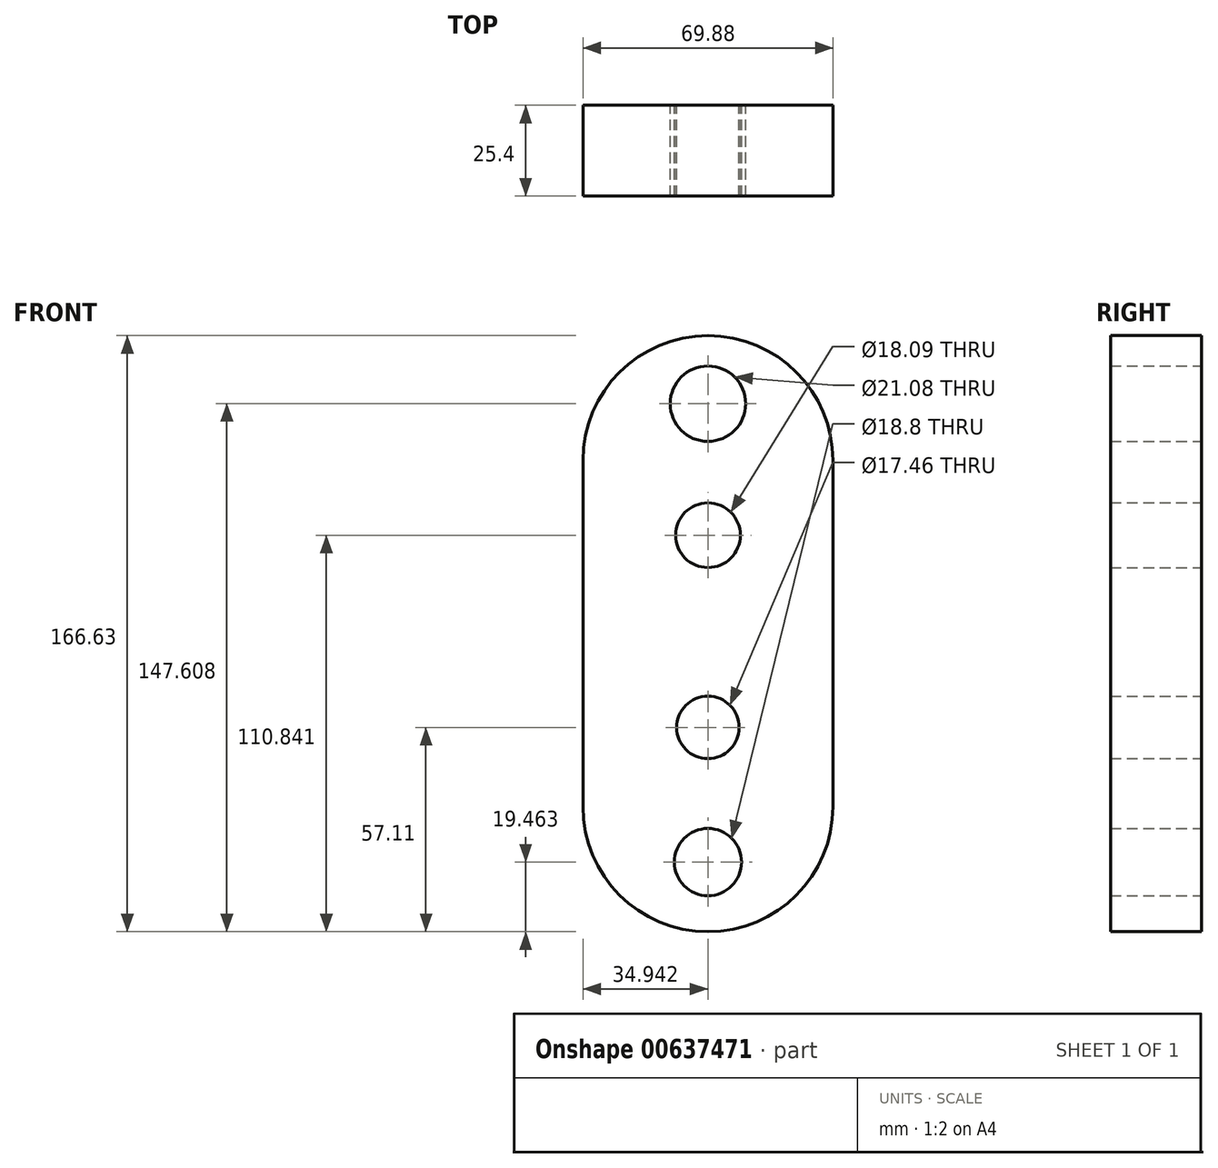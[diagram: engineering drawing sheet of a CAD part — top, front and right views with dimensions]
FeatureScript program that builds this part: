
annotation { "Feature Type Name" : "Feature", "Feature Type Description" : "" }
export const myFeature = defineFeature(function(context is Context, id is Id, definition is map)
    precondition{}
    {
        {
            var Q0;
            Q0=qCreatedBy(makeId("Front.planeOp"),FACE);
            var sketch = newSketch(context, id + "F0", { "sketchPlane" : qUnion([Q0])});
            skLineSegment(sketch, "E0", {"start": v(-48, 38.17) * mm, "end": v(-48, -33.18) * mm});
            skLineSegment(sketch, "E1", {"start": v(-17.47, 38.17) * mm, "end": v(-17.47, -33.18) * mm});
            skArc(sketch, "E2", {"start": v(-17.47, 38.17) * mm, "mid": v(-32.74, 53.44) * mm, "end": v(-48, 38.17) * mm});
            skArc(sketch, "E3", {"start": v(-48, -33.18) * mm, "mid": v(-32.74, -43.31) * mm, "end": v(-17.47, -33.18) * mm});
            skCircle(sketch, "E4", {"center": v(-32.74, 32.6) * mm, "radius": 9.05 * mm});
            skCircle(sketch, "E5", {"center": v(-32.74, -21.14) * mm, "radius": 8.73 * mm});
            skLineSegment(sketch, "E6", {"start": v(-67.68, 53.44) * mm, "end": v(-67.68, -43.31) * mm});
            skPoint(sketch, "E6.startSnap0", {"position": v(-32.74, 53.44) * mm});
            skPoint(sketch, "E6.endSnap0", {"position": v(-32.74, -43.31) * mm});
            skLineSegment(sketch, "E7", {"start": v(2.2, 53.44) * mm, "end": v(2.2, -43.31) * mm});
            skArc(sketch, "E8", {"start": v(2.2, 53.44) * mm, "mid": v(-32.74, 88.38) * mm, "end": v(-67.68, 53.44) * mm});
            skArc(sketch, "E9", {"start": v(-67.68, -43.31) * mm, "mid": v(-32.74, -78.25) * mm, "end": v(2.2, -43.31) * mm});
            skCircle(sketch, "E10", {"center": v(-32.74, 69.36) * mm, "radius": 10.54 * mm});
            skCircle(sketch, "E11", {"center": v(-32.74, -58.79) * mm, "radius": 9.4 * mm});
            skSolve(sketch);
        }
        {
            var Q0;
            Q0 = qSketchRegion(id + "F0", true);
            var Q1;
            Q1=makeQuery(id+"F0.imprint","IMPRINT",FACE,{"disambiguationData":[TD([[makeQuery(id+"F0.imprint","IMPRINT",EDGE,{"derivedFrom":sQuery(id+"F0.wireOp",EDGE,"E0")}),1.0]])]});
            extrude(context, id + "F1", {"entities" : qUnion([Q0, Q1]), "depth" : 25.4 * mm, "offsetDistance" : 25.4 * mm});
        }
    });
